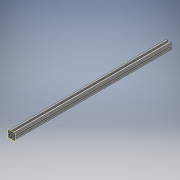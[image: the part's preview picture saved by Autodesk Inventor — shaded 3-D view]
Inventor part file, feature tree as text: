
AUTODESK INVENTOR PART (.ipt)
format: ipt  version: 2016 (Build 200138000, 138)  size: 287,232 bytes
history: native  units: in
note: dims shown in document units (in); Inventor stores cm internally (conversion verified against a paired STEP export)
features: plane x1, split x1, fillet x1
ambient origin geometry x8: Origin, YZ Plane, XZ Plane, XY Plane, X Axis, Y Axis, Z Axis, Center Point
bodies: Solid1 (feature_tree)
feature tree (3):
  plane  "Work Plane1"
  split  "Split1"
  fillet  "Fillet6"  [1 undecoded]
note: 1 required parameter value undecoded (feature->parameter linkage not recoverable at this tier; creation-order binding heuristic only, values carry confidence <= 0.55)
